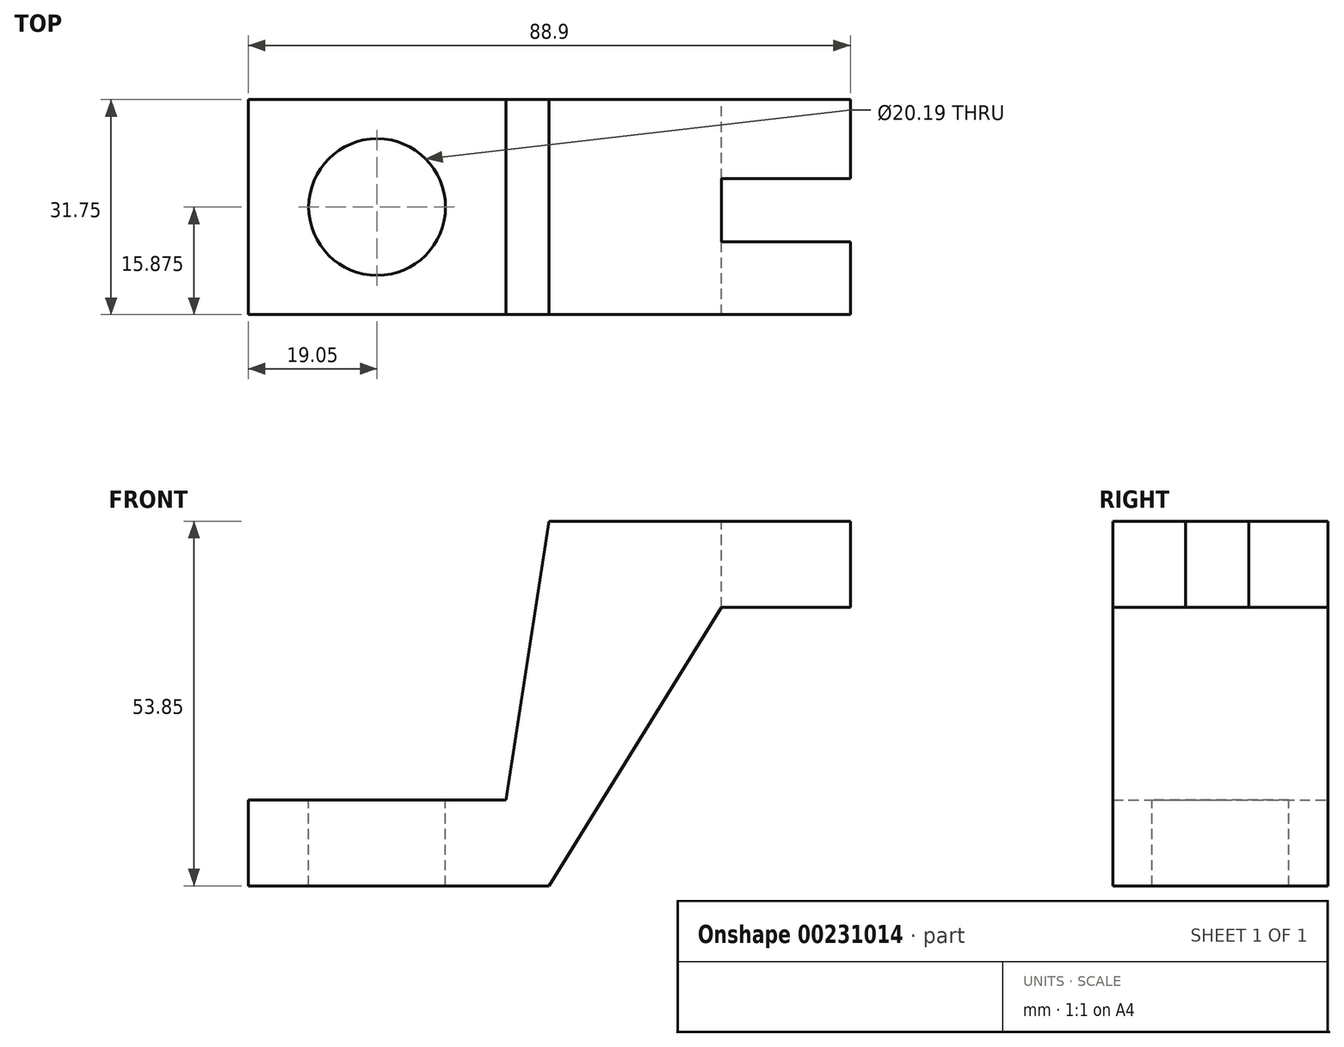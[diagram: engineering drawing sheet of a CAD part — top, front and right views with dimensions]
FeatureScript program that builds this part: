
annotation { "Feature Type Name" : "Feature", "Feature Type Description" : "" }
export const myFeature = defineFeature(function(context is Context, id is Id, definition is map)
    precondition{}
    {
        {
            var Q0;
            Q0=qCreatedBy(makeId("Front.planeOp"),FACE);
            var sketch = newSketch(context, id + "F0", { "sketchPlane" : qUnion([Q0])});
            skLineSegment(sketch, "E0", {"start": v(-44.45, 0) * mm, "end": v(-44.45, -12.7) * mm});
            skLineSegment(sketch, "E1", {"start": v(-44.45, -12.7) * mm, "end": v(0, -12.7) * mm});
            skLineSegment(sketch, "E2", {"start": v(0, -12.7) * mm, "end": v(25.4, 28.45) * mm});
            skLineSegment(sketch, "E3", {"start": v(25.4, 28.45) * mm, "end": v(44.45, 28.45) * mm});
            skLineSegment(sketch, "E4", {"start": v(44.45, 41.15) * mm, "end": v(44.45, 28.45) * mm});
            skLineSegment(sketch, "E5", {"start": v(44.45, 41.15) * mm, "end": v(0, 41.15) * mm});
            skLineSegment(sketch, "E6", {"start": v(0, 41.15) * mm, "end": v(-6.35, 0) * mm});
            skLineSegment(sketch, "E7", {"start": v(-6.35, 0) * mm, "end": v(-44.45, 0) * mm});
            skSolve(sketch);
        }
        {
            var Q0;
            Q0=makeQuery(id+"F0.imprint","IMPRINT",FACE,{"disambiguationData":[TD([[makeQuery(id+"F0.imprint","IMPRINT",EDGE,{"derivedFrom":sQuery(id+"F0.wireOp",EDGE,"E0")}),1.0]])]});
            extrude(context, id + "F1", {"entities" : qUnion([Q0]), "depth" : 31.75 * mm});
        }
        {
            var Q0;
            Q0=makeQuery(id+"F1.opExtrude","SWEPT_FACE",FACE,{"disambiguationData":[OSD([sQuery(id+"F0.wireOp",EDGE,"E7")])]});
            var sketch = newSketch(context, id + "F2", { "sketchPlane" : qUnion([Q0])});
            skCircle(sketch, "E8", {"center": v(-25.4, -15.88) * mm, "radius": 10.1 * mm});
            skSolve(sketch);
        }
        {
            var Q0;
            Q0=makeQuery(id+"F2.imprint","IMPRINT",FACE,{"disambiguationData":[TD([[makeQuery(id+"F2.imprint","IMPRINT",EDGE,{"derivedFrom":sQuery(id+"F2.wireOp",EDGE,"E8")}),1.0]])]});
            extrude(context, id + "F3", {"entities" : qUnion([Q0]), "operationType" : NewBodyOperationType.REMOVE, "oppositeDirection" : true, "depth" : 15.75 * mm});
        }
        {
            var Q0;
            Q0=makeQuery(id+"F1.opExtrude","SWEPT_FACE",FACE,{"disambiguationData":[OSD([sQuery(id+"F0.wireOp",EDGE,"E5")])]});
            var sketch = newSketch(context, id + "F4", { "sketchPlane" : qUnion([Q0])});
            skLineSegment(sketch, "E9", {"start": v(25.4, -21.02) * mm, "end": v(25.4, -11.68) * mm});
            skLineSegment(sketch, "E10", {"start": v(25.4, -11.68) * mm, "end": v(44.45, -11.68) * mm});
            skLineSegment(sketch, "E11", {"start": v(25.4, -21.02) * mm, "end": v(44.45, -21.02) * mm});
            skSolve(sketch);
        }
        {
            var Q0;
            Q0=makeQuery(id+"F4.imprint","IMPRINT",FACE,{"disambiguationData":[TD([[makeQuery(id+"F4.imprint","IMPRINT",EDGE,{"derivedFrom":sQuery(id+"F4.wireOp",EDGE,"E9")}),-1.0]])]});
            extrude(context, id + "F5", {"entities" : qUnion([Q0]), "operationType" : NewBodyOperationType.REMOVE, "oppositeDirection" : true, "depth" : 12.7 * mm});
        }
    });
